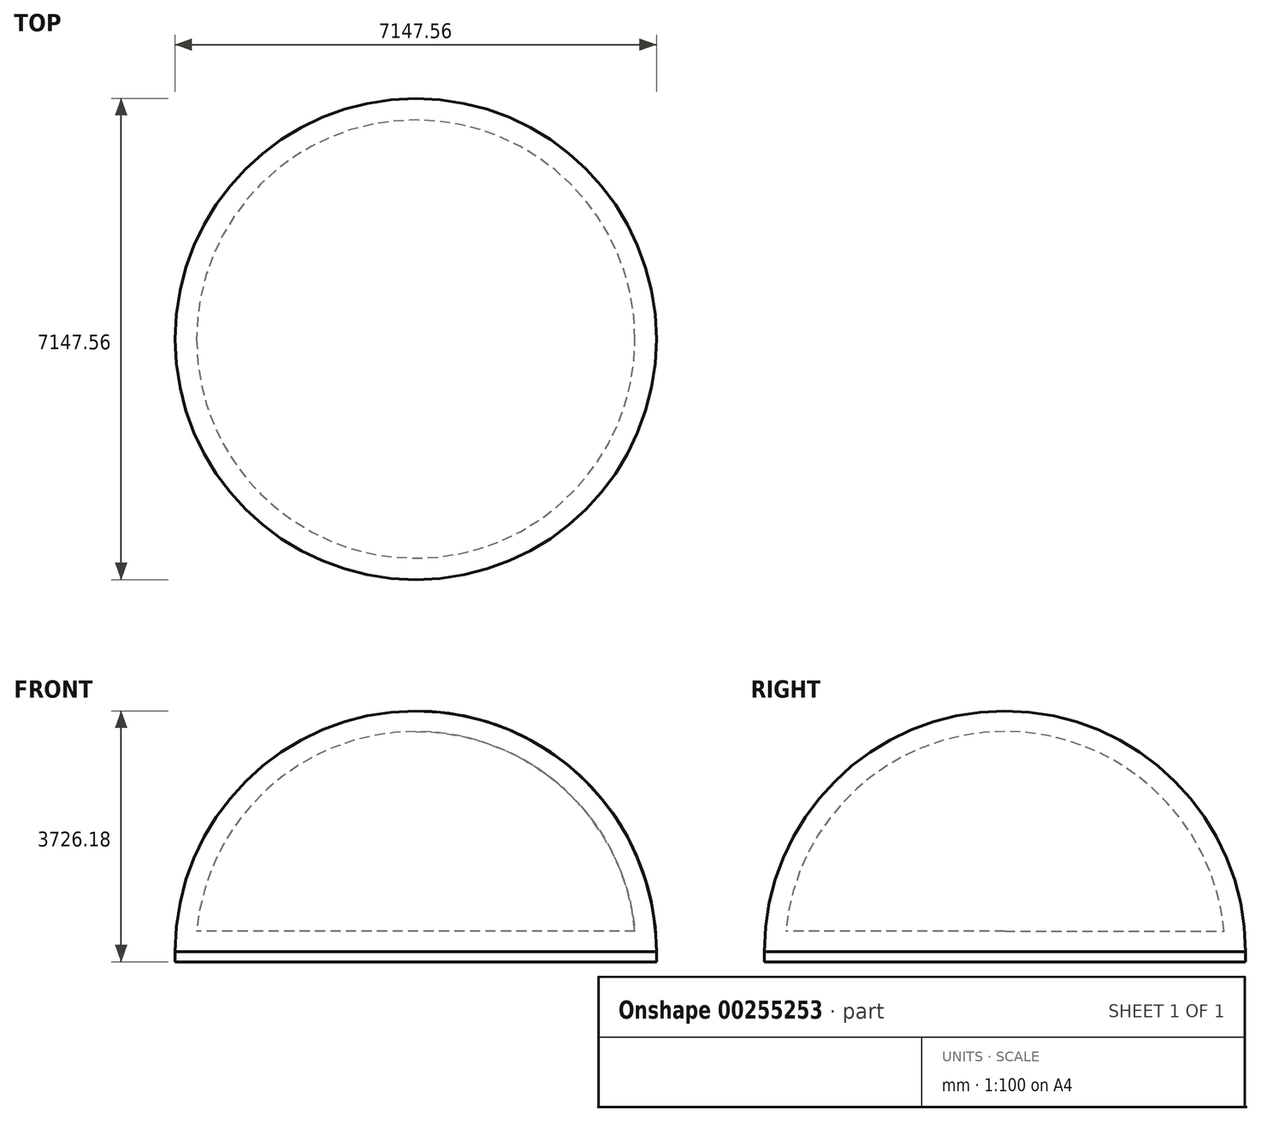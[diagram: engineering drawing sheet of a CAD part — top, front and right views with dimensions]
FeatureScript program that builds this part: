
annotation { "Feature Type Name" : "Feature", "Feature Type Description" : "" }
export const myFeature = defineFeature(function(context is Context, id is Id, definition is map)
    precondition{}
    {
        {
            var Q0;
            Q0=qCreatedBy(makeId("Top.planeOp"),FACE);
            var sketch = newSketch(context, id + "F0", { "sketchPlane" : qUnion([Q0])});
            skCircle(sketch, "E0", {"center": v(0, 0) * mm, "radius": 3573.78 * mm});
            skSolve(sketch);
        }
        {
            var Q0;
            Q0 = qSketchRegion(id + "F0", true);
            extrude(context, id + "F1", {"entities" : qUnion([Q0]), "oppositeDirection" : true, "depth" : 152.4 * mm});
        }
        {
            var Q0;
            Q0=qCreatedBy(makeId("Front.planeOp"),FACE);
            var sketch = newSketch(context, id + "F2", { "sketchPlane" : qUnion([Q0])});
            skArc(sketch, "E1", {"start": v(3573.78, 0) * mm, "mid": v(2527.04, 2527.04) * mm, "end": v(0, 3573.78) * mm});
            skLineSegment(sketch, "E2", {"start": v(0, 0) * mm, "end": v(3573.78, 0) * mm});
            skLineSegment(sketch, "E3", {"start": v(0, 3573.78) * mm, "end": v(0, 3268.98) * mm});
            skPoint(sketch, "E4.orphan", {"position": v(-3573.78, 0) * mm});
            skArc(sketch, "E5.0", {"start": v(3254.74, 304.8) * mm, "mid": v(2201.12, 2416.88) * mm, "end": v(0, 3268.98) * mm});
            skLineSegment(sketch, "E6.0", {"start": v(0, 304.8) * mm, "end": v(3254.74, 304.8) * mm});
            skLineSegment(sketch, "E7.0", {"start": v(304.8, 3573.78) * mm, "end": v(304.8, 3560.76) * mm});
            skLineSegment(sketch, "E8.trimOffspring", {"start": v(3560.76, 304.8) * mm, "end": v(3573.78, 304.8) * mm});
            skLineSegment(sketch, "E9.trimOffspring", {"start": v(0, 304.8) * mm, "end": v(0, 0) * mm});
            skSolve(sketch);
        }
        {
            var Q0;
            Q0=qCreatedBy(makeId("Front.planeOp"),FACE);
            var sketch = newSketch(context, id + "F3", { "sketchPlane" : qUnion([Q0])});
            skLineSegment(sketch, "E10", {"start": v(0, 0) * mm, "end": v(0, 3790.5) * mm, "construction": true});
            skSolve(sketch);
        }
        {
            var Q0;
            Q0 = qSketchRegion(id + "F2", true);
            var Q1;
            Q1=sQuery(id+"F3.wireOp",EDGE,"E10");
            revolve(context, id + "F4", {"entities" : qUnion([Q0]), "axis" : qUnion([Q1]), "revolveType" : RevolveType.FULL});
        }
    });
